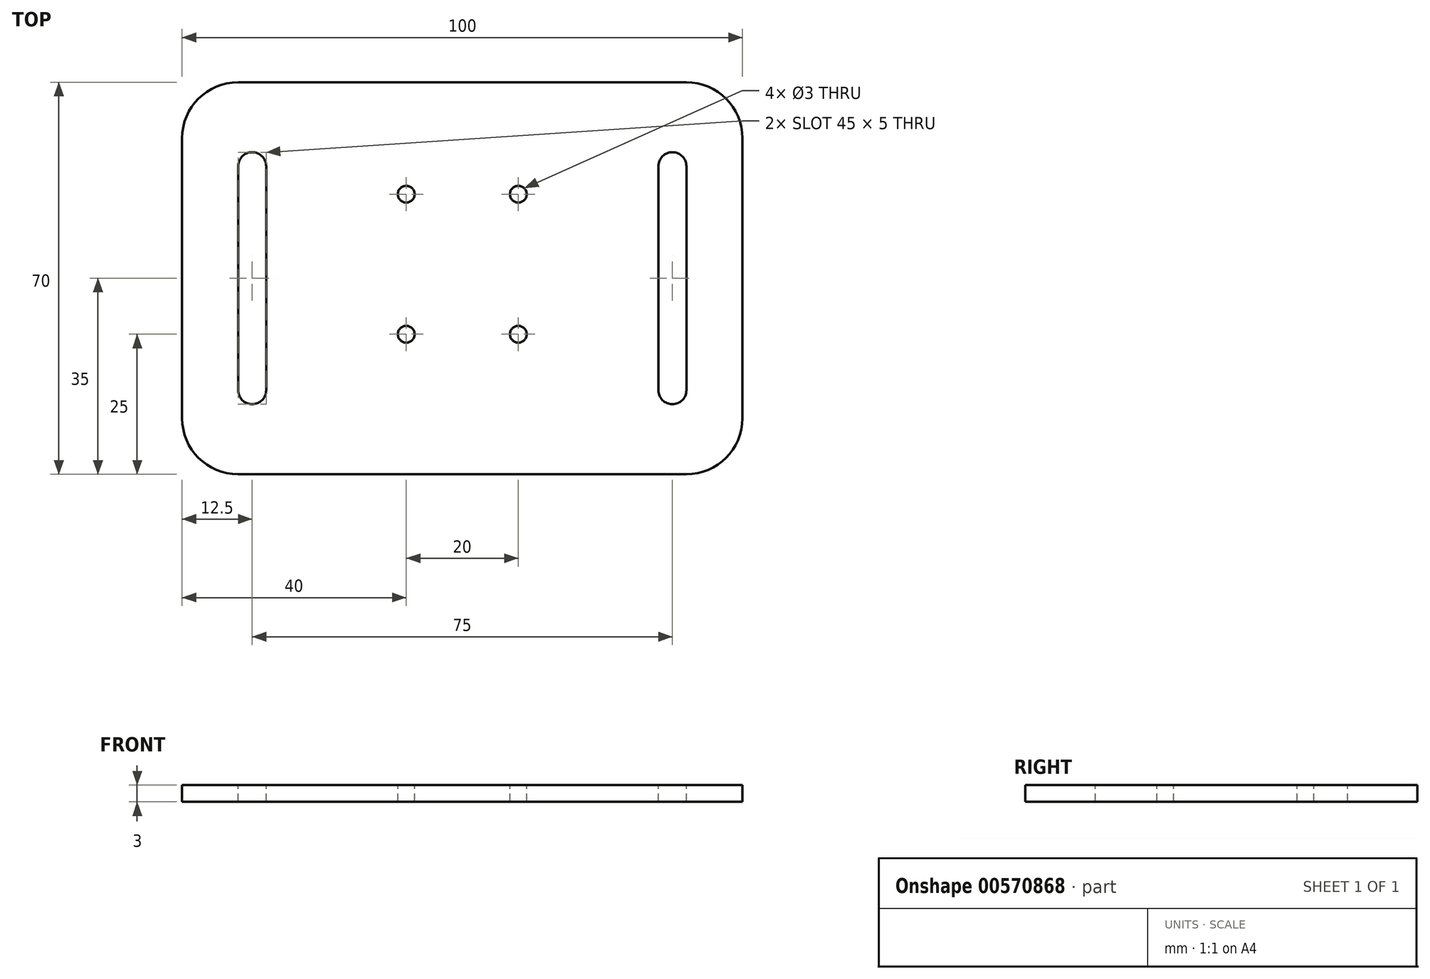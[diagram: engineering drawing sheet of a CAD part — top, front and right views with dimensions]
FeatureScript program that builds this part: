
annotation { "Feature Type Name" : "Feature", "Feature Type Description" : "" }
export const myFeature = defineFeature(function(context is Context, id is Id, definition is map)
    precondition{}
    {
        {
            var Q0;
            Q0=qCreatedBy(makeId("Top.planeOp"),FACE);
            var sketch = newSketch(context, id + "F0", { "sketchPlane" : qUnion([Q0])});
            skLineSegment(sketch, "E0.bottom", {"start": v(0, 0) * mm, "end": v(50, 0) * mm});
            skLineSegment(sketch, "E0.top", {"start": v(0, 70) * mm, "end": v(50, 70) * mm});
            skLineSegment(sketch, "E0.left", {"start": v(0, 0) * mm, "end": v(0, 70) * mm});
            skLineSegment(sketch, "E0.right", {"start": v(50, 0) * mm, "end": v(50, 70) * mm});
            skSolve(sketch);
        }
        {
            var Q0;
            Q0=makeQuery(id+"F0.imprint","IMPRINT",FACE,{"disambiguationData":[TD([[makeQuery(id+"F0.imprint","IMPRINT",EDGE,{"derivedFrom":sQuery(id+"F0.wireOp",EDGE,"E0.bottom")}),1.0]])]});
            extrude(context, id + "F1", {"entities" : qUnion([Q0]), "depth" : 3 * mm, "offsetDistance" : 25 * mm});
        }
        {
            var Q0;
            Q0=makeQuery(id+"F1.opExtrude","CAP_FACE",FACE,{"disambiguationData":[OSD([sQuery(id+"F0.wireOp",EDGE,"E0.bottom"),sQuery(id+"F0.wireOp",EDGE,"E0.top"),sQuery(id+"F0.wireOp",EDGE,"E0.left"),sQuery(id+"F0.wireOp",EDGE,"E0.right")])],"isStart":false});
            var sketch = newSketch(context, id + "F2", { "sketchPlane" : qUnion([Q0])});
            skLineSegment(sketch, "E1", {"start": v(10, 25) * mm, "end": v(10, 50) * mm});
            skSolve(sketch);
        }
        {
            var Q0;
            Q0=makeQuery(id+"F2.imprint","IMPRINT",FACE,{"disambiguationData":[TD([[makeQuery(id+"F2.imprint","IMPRINT",EDGE,{"derivedFrom":makeQuery(id+"F1.opExtrude","CAP_EDGE",EDGE,{"disambiguationData":[OSD([sQuery(id+"F0.wireOp",EDGE,"E0.bottom")])],"isStart":false})}),1.0]])]});
            var sketch = newSketch(context, id + "F3", { "sketchPlane" : qUnion([Q0])});
            skSolve(sketch);
        }
        {
            var Q0;
            Q0=sQuery(id+"F2.wireOp",VERTEX,"E1.start");
            var Q1;
            Q1=sQuery(id+"F2.wireOp",VERTEX,"E1.end");
            var Q2;
            Q2=makeQuery(id+"F1.opExtrude","SWEPT_BODY",BODY,{"disambiguationData":[OSD([sQuery(id+"F0.wireOp",EDGE,"E0.bottom"),sQuery(id+"F0.wireOp",EDGE,"E0.top"),sQuery(id+"F0.wireOp",EDGE,"E0.left"),sQuery(id+"F0.wireOp",EDGE,"E0.right")])]});
            hole(context, id + "F4", {"style" : HoleStyle.SIMPLE, "endStyle" : HoleEndStyle.THROUGH, "holeDiameter" : 3 * mm, "isTappedThrough" : true, "tappedDepth" : 12 * mm, "tapClearance" : 3, "locations" : qUnion([Q0, Q1]), "scope" : qUnion([Q2])});
        }
        {
            var Q0;
            Q0=makeQuery(id+"F3.imprint","IMPRINT",FACE,{"disambiguationData":[TD([[makeQuery(id+"F3.imprint","IMPRINT",EDGE,{"derivedFrom":makeQuery(id+"F2.imprint","IMPRINT",EDGE,{"derivedFrom":makeQuery(id+"F1.opExtrude","CAP_EDGE",EDGE,{"disambiguationData":[OSD([sQuery(id+"F0.wireOp",EDGE,"E0.bottom")])],"isStart":false})})}),1.0]])]});
            var sketch = newSketch(context, id + "F5", { "sketchPlane" : qUnion([Q0])});
            skLineSegment(sketch, "E2", {"start": v(37.5, 15) * mm, "end": v(37.5, 55) * mm});
            skSolve(sketch);
        }
        {
            var Q0;
            Q0=makeQuery(id+"F5.imprint","IMPRINT",FACE,{"disambiguationData":[TD([[makeQuery(id+"F5.imprint","IMPRINT",EDGE,{"derivedFrom":makeQuery(id+"F3.imprint","IMPRINT",EDGE,{"derivedFrom":makeQuery(id+"F2.imprint","IMPRINT",EDGE,{"derivedFrom":makeQuery(id+"F1.opExtrude","CAP_EDGE",EDGE,{"disambiguationData":[OSD([sQuery(id+"F0.wireOp",EDGE,"E0.bottom")])],"isStart":false})})})}),1.0]])]});
            var sketch = newSketch(context, id + "F6", { "sketchPlane" : qUnion([Q0])});
            skSolve(sketch);
        }
        {
            var Q0;
            Q0=makeQuery(id+"F6.imprint","IMPRINT",FACE,{"disambiguationData":[TD([[makeQuery(id+"F6.imprint","IMPRINT",EDGE,{"derivedFrom":makeQuery(id+"F5.imprint","IMPRINT",EDGE,{"derivedFrom":makeQuery(id+"F3.imprint","IMPRINT",EDGE,{"derivedFrom":makeQuery(id+"F2.imprint","IMPRINT",EDGE,{"derivedFrom":makeQuery(id+"F1.opExtrude","CAP_EDGE",EDGE,{"disambiguationData":[OSD([sQuery(id+"F0.wireOp",EDGE,"E0.bottom")])],"isStart":false})})})})}),1.0]])]});
            var sketch = newSketch(context, id + "F7", { "sketchPlane" : qUnion([Q0])});
            skLineSegment(sketch, "E3.JWB.JWB", {"start": v(37.5, 15) * mm, "end": v(37.5, 55) * mm, "construction": true});
            skArc(sketch, "E3.0.startCap", {"start": v(40, 15) * mm, "mid": v(37.5, 12.5) * mm, "end": v(35, 15) * mm});
            skArc(sketch, "E3.0.endCap", {"start": v(35, 55) * mm, "mid": v(37.5, 57.5) * mm, "end": v(40, 55) * mm});
            skLineSegment(sketch, "E3.0.left", {"start": v(35, 15) * mm, "end": v(35, 55) * mm});
            skLineSegment(sketch, "E3.0.right", {"start": v(40, 15) * mm, "end": v(40, 55) * mm});
            skSolve(sketch);
        }
        {
            var Q0;
            Q0 = qSketchRegion(id + "F7", true);
            extrude(context, id + "F8", {"entities" : qUnion([Q0]), "operationType" : NewBodyOperationType.REMOVE, "oppositeDirection" : true, "depth" : 28.64 * mm, "offsetDistance" : 25 * mm});
        }
        {
            var Q0;
            Q0=makeQuery(id+"F1.opExtrude","SWEPT_EDGE",EDGE,{"disambiguationData":[OSD([sQuery(id+"F0.wireOp",EDGE,"E0.top"),sQuery(id+"F0.wireOp",EDGE,"E0.right")])]});
            var Q1;
            Q1=makeQuery(id+"F1.opExtrude","SWEPT_EDGE",EDGE,{"disambiguationData":[OSD([sQuery(id+"F0.wireOp",EDGE,"E0.bottom"),sQuery(id+"F0.wireOp",EDGE,"E0.right")])]});
            fillet(context, id + "F9", {"entities" : qUnion([Q0, Q1]), "radius" : 10 * mm, "tangentPropagation" : true, "allowEdgeOverflow" : false});
        }
        {
            var Q0;
            Q0=makeQuery(id+"F1.opExtrude","SWEPT_BODY",BODY,{"disambiguationData":[OSD([sQuery(id+"F0.wireOp",EDGE,"E0.bottom"),sQuery(id+"F0.wireOp",EDGE,"E0.top"),sQuery(id+"F0.wireOp",EDGE,"E0.left"),sQuery(id+"F0.wireOp",EDGE,"E0.right")])]});
            var Q1;
            Q1=qCreatedBy(makeId("Right.planeOp"),FACE);
            mirror(context, id + "F10", {"operationType" : NewBodyOperationType.ADD, "entities" : qUnion([Q0]), "mirrorPlane" : qUnion([Q1])});
        }
    });
